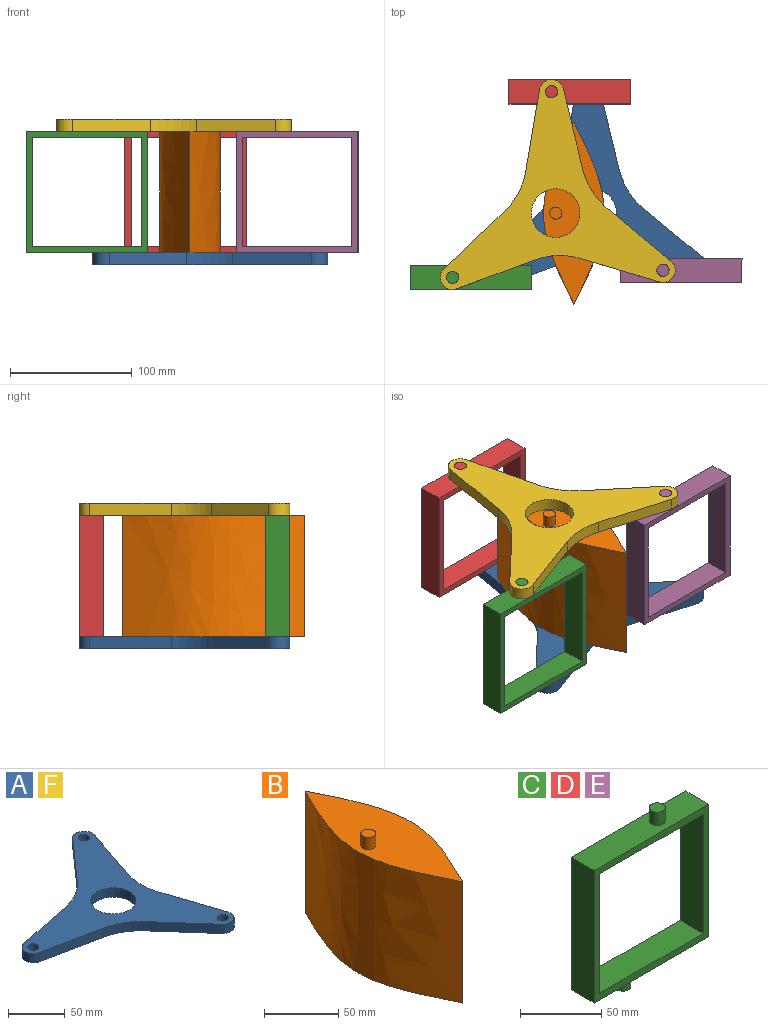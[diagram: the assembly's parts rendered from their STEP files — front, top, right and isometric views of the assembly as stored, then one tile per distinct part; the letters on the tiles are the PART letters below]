
ASSEMBLY  parts=6 mates=8
PART A: 18 faces, bbox 170x193.2x10 mm
  f0: plane 66.56x13.59mm, normal (-0.2,0.98,0), area 679.3mm2, adj f1,f13,f14,f15
  f1: cylinder r=10mm len=19.6mm, axis (0,0,-1), area 273.9mm2, adj f0,f2,f13,f14
  f2: plane 66.56x13.59mm, normal (-0.2,-0.98,0), area 679.3mm2, adj f1,f13,f14,f16
  f3: plane 50.85x45.05mm, normal (-0.75,-0.66,0), area 679.3mm2, adj f4,f13,f14,f16
  f4: cylinder r=10mm len=17.49mm, axis (0,0,-1), area 273.9mm2, adj f3,f5,f13,f14
  f5: plane 64.43x21.51mm, normal (0.95,0.32,0), area 679.3mm2, adj f4,f13,f14,f17
  f6: plane 64.43x21.51mm, normal (0.95,-0.32,0), area 679.3mm2, adj f7,f13,f14,f17
  f7: cylinder r=10mm len=17.49mm, axis (0,0,-1), area 273.9mm2, adj f6,f10,f13,f14
  f8: cylinder r=20mm len=40mm, axis (0,0,-1), area 1256.6mm2, adj f13,f14
  f9: cylinder r=5mm len=10mm, axis (0,0,-1), area 314.2mm2, adj f13,f14
  f10: plane 50.85x45.05mm, normal (-0.75,0.66,0), area 679.3mm2, adj f7,f13,f14,f15
  f11: cylinder r=5mm len=10mm, axis (0,0,-1), area 314.2mm2, adj f13,f14
  f12: cylinder r=5mm len=10mm, axis (0,0,-1), area 314.2mm2, adj f13,f14
  f13: plane 193.21x170mm, normal (0,0,1), area 9900.3mm2, adj f0,f1,f2,f3,f4,f5,f6,f7
  f14: plane 193.21x170mm, normal (0,0,-1), area 9900.3mm2, adj f0,f1,f2,f3,f4,f5,f6,f7
  f15: cylinder r=60mm len=32.91mm, axis (0,0,1), area 386.7mm2, adj f0,f10,f13,f14
  f16: cylinder r=60mm len=32.91mm, axis (0,0,1), area 386.7mm2, adj f2,f3,f13,f14
  f17: cylinder r=60mm len=38mm, axis (0,0,-1), area 386.7mm2, adj f5,f6,f13,f14
PART B: 8 faces, bbox 52.6x150x120 mm
  f0: cylinder r=5mm len=10mm, axis (0,0,-1), area 314.2mm2, adj f1,f2
  f1: plane 10x10mm, normal (0,0,1), area 78.5mm2, adj f0
  f2: plane 150x52.6mm, normal (0,0,1), area 4608.9mm2, adj f0,f3,f4
  f3: extruded ~150x100mm, area 15956.8mm2, adj f2,f4,f7
  f4: extruded ~150x100mm, area 15956.8mm2, adj f2,f3,f7
  f5: plane 10x10mm, normal (0,0,-1), area 78.5mm2, adj f6
  f6: cylinder r=5mm len=10mm, axis (0,0,1), area 314.2mm2, adj f5,f7
  f7: plane 150x52.6mm, normal (0,0,-1), area 4608.9mm2, adj f3,f4,f6
PART C: 14 faces, bbox 100x20x120 mm
  f0: plane 100x20mm, normal (0,0,1), area 1921.5mm2, adj f1,f7,f8,f9,f10
  f1: plane 100x20mm, normal (-1,0,0), area 2000mm2, adj f0,f2,f8,f9
  f2: plane 100x20mm, normal (0,0,-1), area 1921.5mm2, adj f1,f7,f8,f9,f12
  f3: plane 90x20mm, normal (1,0,0), area 1800mm2, adj f4,f6,f8,f9
  f4: plane 90x20mm, normal (0,0,-1), area 1800mm2, adj f3,f5,f8,f9
  f5: plane 90x20mm, normal (-1,0,0), area 1800mm2, adj f4,f6,f8,f9
  f6: plane 90x20mm, normal (0,0,1), area 1800mm2, adj f3,f5,f8,f9
  f7: plane 100x20mm, normal (1,0,0), area 2000mm2, adj f0,f2,f8,f9
  f8: plane 100x100mm, normal (0,-1,0), area 1900mm2, adj f0,f1,f2,f3,f4,f5,f6,f7
  f9: plane 100x100mm, normal (0,1,0), area 1900mm2, adj f0,f1,f2,f3,f4,f5,f6,f7
  f10: cylinder r=5mm len=10mm, axis (0,0,-1), area 314.2mm2, adj f0,f11
  f11: plane 10x10mm, normal (0,0,1), area 78.5mm2, adj f10
  f12: cylinder r=5mm len=10mm, axis (0,0,1), area 314.2mm2, adj f2,f13
  f13: plane 10x10mm, normal (0,0,-1), area 78.5mm2, adj f12
PART D: same geometry as C
PART E: same geometry as C
PART F: same geometry as A
PLACE A rot(axis=(0,0,-1),88deg) t=(15,0,-10)mm
PLACE B at identity fixed
PLACE C rot(axis=(0,0,-1),180deg) t=(-84.85,-52.93,50)mm
PLACE D rot(axis=(0,0,1),180deg) t=(-3.41,99.94,50)mm
PLACE E rot(axis=(0,0,1),180deg) t=(88.26,-47.01,50)mm
PLACE F rot(axis=(0,0,-1),88deg) t=(-15,0,100)mm
MATE revolute C.f12 <-> A.f4  axis (0,0,-1) through (-69.85,-52.93,-10)mm
MATE revolute E.f10 <-> F.f7  axis (0,0,1) through (73.26,-47.01,110)mm
MATE revolute D.f10 <-> F.f11  axis (0,0,1) through (-18.41,99.94,110)mm
MATE parallel D.f7 <-> E.f7  axis (-1,0,0) through (-53.41,99.94,50)mm
MATE revolute C.f10 <-> F.f4  axis (0,0,1) through (-99.85,-52.93,110)mm
MATE revolute E.f12 <-> A.f7  axis (0,0,-1) through (103.26,-47.01,-10)mm
MATE revolute F.f8 <-> B.f0  axis (0,0,1) through (-15,0,110)mm
MATE revolute A.f8 <-> B.f6  axis (0,0,-1) through (15,0,-10)mm
